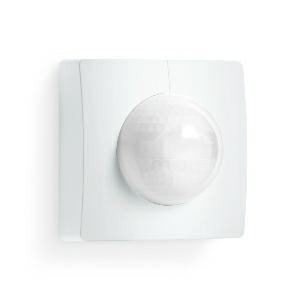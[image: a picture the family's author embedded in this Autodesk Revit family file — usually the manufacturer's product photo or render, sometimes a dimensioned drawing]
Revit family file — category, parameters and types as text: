
# Revit family: is_3180_057350
name_source: partatom
category: Elektroinstallationen
revit_build: Autodesk Revit 2016 (Build: 20190508_0715(x64)
units: mm (PartAtom-declared; Revit-internal decimal feet)

## family parameters
Basisbauteil = Fläche
Beim Laden mit Abzugskörper schneiden = Nein
Bemaßung runder Anschluss = Durchmesser verwenden
Beschriftungsausrichtung beibehalten = Nein
Gemeinsam genutzt = Nein
Raumberechnungspunkt = Nein
Teiletyp = Normal

## types (1)
- IS 3180
    Apparent Load = 0 VA
    Beschreibung = Type: Motion detectors; Dimensions (L x W x H): 65 x 95 x 95 mm; Mains power supply: 12 – 22,5 V / 50 – 60 Hz; Sensor Technology: passive infrared; Application, place: Outdoors, Indoors; Application, room: corridor / aisle, function room / ancillary room, stairwell, multi-storey / underground car park, outdoors, all round the building, courtyard & driveway, Indoors; Installation site: wall, corner; Installation: Surface wiring; Switching zones: 448 switching zones; Electronic scalability: No; Mechanical scalability: No; Mounting height: 1,80 – 2,50 m; Optimum mounting height: 2 m; Detection angle: 180 °; Angle of aperture: 90 °; Sneak-by guard: Yes; Capability of masking out individual segments: Yes; Reach, radial: r = 4.5 m (32 m²); Reach, tangential: r = 20 m (628 m²); Twilight setting TEACH: Yes; Twilight setting: 2 – 1000 lx; Switching output 1, floating: No; Control output, Dali: Addressable/slave; Basic light level function: No; With bus coupling: Yes; Settings via: Bus; With remote control: No; Interconnection: Yes; IP-rating: IP54; Material: Plastic; Ambient temperature: -20 – 50 °C; Colour: white; Colour, RAL: 9003; Manufacturer's Warranty: 5 years; Version: DALI-2 IPD - surface, sq.; PU1, EAN: 4007841057350
    Height = 95 mm
    Hersteller = Steinel
    Length = 65 mm
    Maximum range = 22.153 m
    ModVariant = Nein
    Modell = 057350
    Mounting Type = Surface mounted
    Number of Poles = 1
    OnlyDefault = Ja
    Power Factor = 1
    Product Name = IS 3180
    Product group = Sensor-switched indoor light
    ProductGroupID = 30
    Protection Class = Protection class
    Protection Degree = IP 54
    RlxData = <blob elided: 166961 chars, md5=4342c57f>
    Sensor characteristics = Semi circular 145°-300°
    Sensor type = Passive (infrared)
    SensorDataFile = <blob elided: 5082 chars, md5=d953030a>
    Type of entry = Motion
    Typenbild = produkt1_057350.jpg
    Typenkommentare = Product without accessories
    URL = http://relux.com
    VarID = ---
    Voltage = 0 V
    Vorgabe-Ansicht = 1800 mm
    Weight = 0.00 kg
    Width = 95 mm

## geometry (parser evidence)
native form markers: Sweep x16
no freeform markers — native parametric forms only
